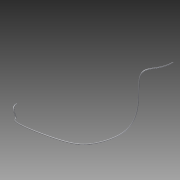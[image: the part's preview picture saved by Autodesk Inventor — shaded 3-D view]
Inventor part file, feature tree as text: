
AUTODESK INVENTOR PART (.ipt)
format: ipt  version: 2012 (Build 160160000, 160)  size: 122,368 bytes
history: native  units: in
note: dims shown in document units (in); Inventor stores cm internally (conversion verified against a paired STEP export)
features: sketch x2, sweep x1
ambient origin geometry x8: Origin, YZ Plane, XZ Plane, XY Plane, X Axis, Y Axis, Z Axis, Center Point
bodies: Solid1 (feature_tree)
feature tree (3):
  sweep  "Sweep1"
  sketch  "Sketch1"  dims[d0=0.0787in d1=0.0in]
  sketch  "3D Sketch1"
